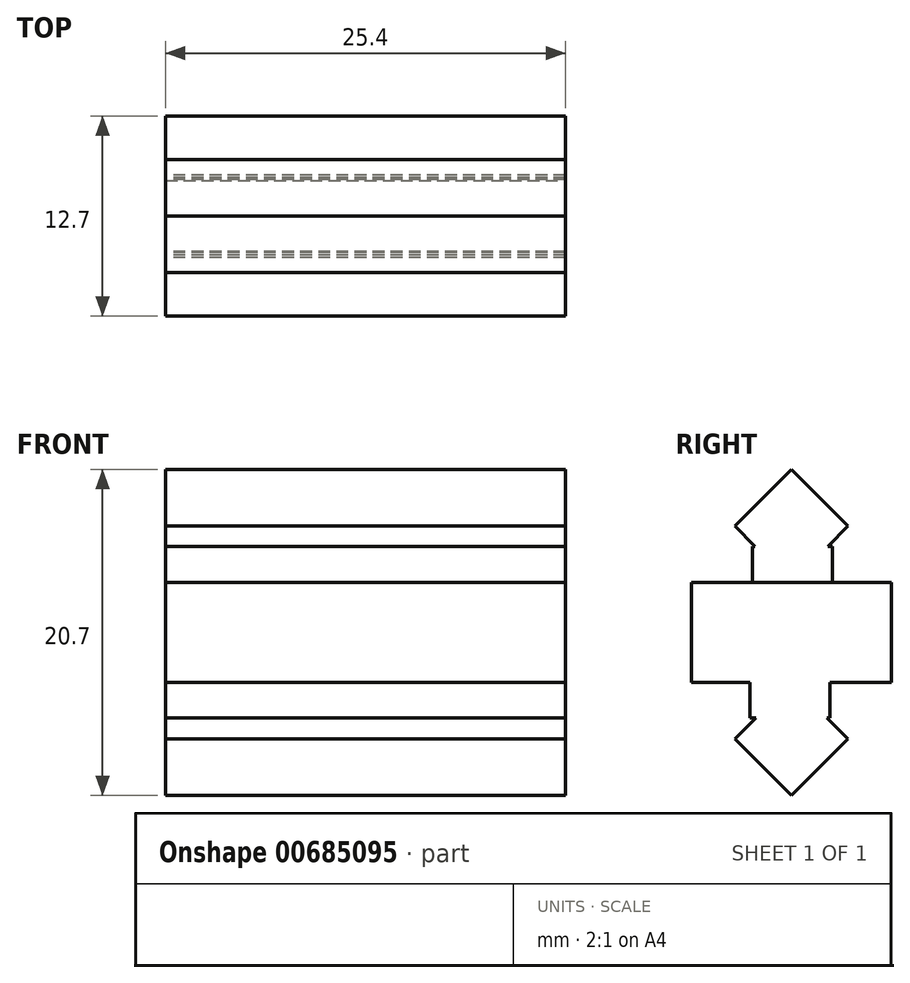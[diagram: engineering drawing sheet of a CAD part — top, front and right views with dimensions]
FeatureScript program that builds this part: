
annotation { "Feature Type Name" : "Feature", "Feature Type Description" : "" }
export const myFeature = defineFeature(function(context is Context, id is Id, definition is map)
    precondition{}
    {
        {
            var Q0;
            Q0=qCreatedBy(makeId("Top.planeOp"),FACE);
            var sketch = newSketch(context, id + "F0", { "sketchPlane" : qUnion([Q0])});
            skLineSegment(sketch, "E0.bottom", {"start": v(12.7, -6.35) * mm, "end": v(-12.7, -6.35) * mm});
            skLineSegment(sketch, "E0.top", {"start": v(12.7, 6.35) * mm, "end": v(-12.7, 6.35) * mm});
            skLineSegment(sketch, "E0.left", {"start": v(12.7, -6.35) * mm, "end": v(12.7, 6.35) * mm});
            skLineSegment(sketch, "E0.right", {"start": v(-12.7, -6.35) * mm, "end": v(-12.7, 6.35) * mm});
            skPoint(sketch, "E0.middle", {"position": v(0, 0) * mm});
            skSolve(sketch);
        }
        {
            var Q0;
            Q0=qCreatedBy(makeId("Right.planeOp"),FACE);
            var sketch = newSketch(context, id + "F1", { "sketchPlane" : qUnion([Q0])});
            skLineSegment(sketch, "E1.bottom", {"start": v(0, 10.35) * mm, "end": v(3.6, 6.75) * mm});
            skLineSegment(sketch, "E1.top", {"start": v(-3.6, 6.75) * mm, "end": v(0, 3.16) * mm});
            skLineSegment(sketch, "E1.left", {"start": v(0, 10.35) * mm, "end": v(-3.6, 6.75) * mm});
            skLineSegment(sketch, "E1.right", {"start": v(3.6, 6.75) * mm, "end": v(0, 3.16) * mm});
            skSolve(sketch);
        }
        {
            var Q0;
            Q0=qCreatedBy(makeId("Right.planeOp"),FACE);
            var sketch = newSketch(context, id + "F2", { "sketchPlane" : qUnion([Q0])});
            skLineSegment(sketch, "E2.bottom", {"start": v(3.6, -6.75) * mm, "end": v(0, -3.16) * mm});
            skLineSegment(sketch, "E2.top", {"start": v(0, -10.35) * mm, "end": v(-3.6, -6.75) * mm});
            skLineSegment(sketch, "E2.left", {"start": v(3.6, -6.75) * mm, "end": v(0, -10.35) * mm});
            skLineSegment(sketch, "E2.right", {"start": v(0, -3.16) * mm, "end": v(-3.6, -6.75) * mm});
            skSolve(sketch);
        }
        {
            var Q0;
            Q0=makeQuery(id+"F0.imprint","IMPRINT",FACE,{"disambiguationData":[TD([[makeQuery(id+"F0.imprint","IMPRINT",EDGE,{"derivedFrom":sQuery(id+"F0.wireOp",EDGE,"E0.bottom")}),-1.0]])]});
            extrude(context, id + "F3", {"entities" : qUnion([Q0]), "depth" : 3.17 * mm, "offsetDistance" : 25.4 * mm});
        }
        {
            var Q0;
            Q0=makeQuery(id+"F3.opExtrude","CAP_FACE",FACE,{"disambiguationData":[OSD([sQuery(id+"F0.wireOp",EDGE,"E0.bottom"),sQuery(id+"F0.wireOp",EDGE,"E0.top"),sQuery(id+"F0.wireOp",EDGE,"E0.left"),sQuery(id+"F0.wireOp",EDGE,"E0.right")])],"isStart":true});
            extrude(context, id + "F4", {"entities" : qUnion([Q0]), "operationType" : NewBodyOperationType.ADD, "depth" : 3.17 * mm, "offsetDistance" : 25.4 * mm});
        }
        {
            var Q0;
            Q0=qCreatedBy(makeId("Right.planeOp"),FACE);
            var sketch = newSketch(context, id + "F5", { "sketchPlane" : qUnion([Q0])});
            skLineSegment(sketch, "E3.bottom", {"start": v(2.6, 5.47) * mm, "end": v(-2.47, 5.47) * mm});
            skLineSegment(sketch, "E3.top", {"start": v(2.6, 3.19) * mm, "end": v(-2.47, 3.19) * mm});
            skLineSegment(sketch, "E3.left", {"start": v(2.6, 5.47) * mm, "end": v(2.6, 3.19) * mm});
            skLineSegment(sketch, "E3.right", {"start": v(-2.47, 5.47) * mm, "end": v(-2.47, 3.19) * mm});
            skSolve(sketch);
        }
        {
            var Q0;
            Q0=qCreatedBy(makeId("Right.planeOp"),FACE);
            var sketch = newSketch(context, id + "F6", { "sketchPlane" : qUnion([Q0])});
            skLineSegment(sketch, "E4.bottom", {"start": v(2.45, -3.13) * mm, "end": v(-2.63, -3.13) * mm});
            skLineSegment(sketch, "E4.top", {"start": v(2.45, -5.42) * mm, "end": v(-2.63, -5.42) * mm});
            skLineSegment(sketch, "E4.left", {"start": v(2.45, -3.13) * mm, "end": v(2.45, -5.42) * mm});
            skLineSegment(sketch, "E4.right", {"start": v(-2.63, -3.13) * mm, "end": v(-2.63, -5.42) * mm});
            skSolve(sketch);
        }
        {
            var Q0;
            Q0=makeQuery(id+"F1.imprint","IMPRINT",FACE,{"disambiguationData":[TD([[makeQuery(id+"F1.imprint","IMPRINT",EDGE,{"derivedFrom":sQuery(id+"F1.wireOp",EDGE,"E1.bottom")}),-1.0]])]});
            var Q1;
            Q1=makeQuery(id+"F5.imprint","IMPRINT",FACE,{"disambiguationData":[TD([[makeQuery(id+"F5.imprint","IMPRINT",EDGE,{"derivedFrom":sQuery(id+"F5.wireOp",EDGE,"E3.bottom")}),1.0]])]});
            extrude(context, id + "F7", {"entities" : qUnion([Q0, Q1]), "operationType" : NewBodyOperationType.ADD, "depth" : 12.7 * mm, "offsetDistance" : 25.4 * mm});
        }
        {
            var Q0;
            Q0=makeQuery(id+"F6.imprint","IMPRINT",FACE,{"disambiguationData":[TD([[makeQuery(id+"F6.imprint","IMPRINT",EDGE,{"derivedFrom":sQuery(id+"F6.wireOp",EDGE,"E4.bottom")}),1.0]])]});
            var Q1;
            Q1=makeQuery(id+"F2.imprint","IMPRINT",FACE,{"disambiguationData":[TD([[makeQuery(id+"F2.imprint","IMPRINT",EDGE,{"derivedFrom":sQuery(id+"F2.wireOp",EDGE,"E2.bottom")}),1.0]])]});
            extrude(context, id + "F8", {"entities" : qUnion([Q0, Q1]), "operationType" : NewBodyOperationType.ADD, "depth" : 12.7 * mm, "offsetDistance" : 25.4 * mm});
        }
        {
            var Q0;
            Q0=makeQuery(id+"F7.boolean.opBoolean","MERGE",FACE,{"derivedFrom":[makeQuery(id+"F7.opExtrude","CAP_FACE",FACE,{"disambiguationData":[OSD([sQuery(id+"F1.wireOp",EDGE,"E1.bottom"),sQuery(id+"F1.wireOp",EDGE,"E1.top"),sQuery(id+"F1.wireOp",EDGE,"E1.left"),sQuery(id+"F1.wireOp",EDGE,"E1.right")])],"isStart":true}),makeQuery(id+"F7.opExtrude","CAP_FACE",FACE,{"disambiguationData":[OSD([sQuery(id+"F5.wireOp",EDGE,"E3.bottom"),sQuery(id+"F5.wireOp",EDGE,"E3.top"),sQuery(id+"F5.wireOp",EDGE,"E3.left"),sQuery(id+"F5.wireOp",EDGE,"E3.right")])],"isStart":true})]});
            var Q1;
            Q1=makeQuery(id+"F8.boolean.opBoolean","MERGE",FACE,{"derivedFrom":[makeQuery(id+"F8.opExtrude","CAP_FACE",FACE,{"disambiguationData":[OSD([sQuery(id+"F2.wireOp",EDGE,"E2.bottom"),sQuery(id+"F2.wireOp",EDGE,"E2.top"),sQuery(id+"F2.wireOp",EDGE,"E2.left"),sQuery(id+"F2.wireOp",EDGE,"E2.right")])],"isStart":true}),makeQuery(id+"F8.opExtrude","CAP_FACE",FACE,{"disambiguationData":[OSD([sQuery(id+"F6.wireOp",EDGE,"E4.bottom"),sQuery(id+"F6.wireOp",EDGE,"E4.top"),sQuery(id+"F6.wireOp",EDGE,"E4.left"),sQuery(id+"F6.wireOp",EDGE,"E4.right")])],"isStart":true})]});
            extrude(context, id + "F9", {"entities" : qUnion([Q0, Q1]), "operationType" : NewBodyOperationType.ADD, "depth" : 12.7 * mm, "offsetDistance" : 25.4 * mm});
        }
    });
